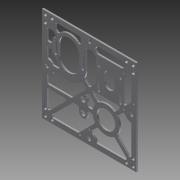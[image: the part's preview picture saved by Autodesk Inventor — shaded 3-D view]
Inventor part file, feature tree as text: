
AUTODESK INVENTOR PART (.ipt)
format: ipt  version: 2012 (Build 160160000, 160)  size: 569,856 bytes
history: native  units: in
note: dims shown in document units (in); Inventor stores cm internally (conversion verified against a paired STEP export)
features: fillet x6, hole x5, extrude x4, sketch x1, chamfer x1
ambient origin geometry x8: Origin, YZ Plane, XZ Plane, XY Plane, X Axis, Y Axis, Z Axis, Center Point
feature tree (17):
  sketch  "Sketch1"  dims[d0=4.5in d1=7.0in d2=7.0in d3=4.5in d4=1.375in d5=2.25in d6=2.25in d10=0.125in d12=0.125in d15=0.25in d16=0.75in d19=0.25in d20=0.75in d23=0.125in d24=0.25in d25=0.75in d26=0.125in d27=0.25in d28=0.25in d29=0.25in d30=0.75in d34=0.125in d35=0.25in d36=0.25in d37=0.25in d38=0.75in d39=0.125in d40=0.125in d47=0.125in d48=0.25in d49=0.25in d50=0.125in d51=0.75in d52=0.25in d87=1.5in d88=1.625in d89=1.5in d91=2.0in d95=0.75in d98=1.0in d99=1.0in d140=1.0in d141=1.0in d142=1.0in d143=1.0in d167=0.375in d168=0.375in d169=1.25in d171=6.25in d172=6.25in d173=0.375in d174=0.375in d177=3.625in d180=45.0deg d182=0.25in d183=0.25in d186=0.25in d188=0.25in d190=0.125in d195=0.125in d197=0.125in d198=0.25in d204=0.125in d205=0.125in d206=0.25in d207=0.125in d217=0.125in d218=3.5in d220=0.5in d221=1.375in d222=0.5in d223=1.375in d224=0.125in d225=0.0in d226=0.125in d227=0.2in d228=0.75in d229=0.375in d230=0.25in d231=0.5635in d232=1.0in d233=0.8108in d234=1.75in d235=1.0in d236=0.125in d237=0.75in d238=0.375in d239=0.25in d240=0.5635in d241=1.0in d242=0.8108in d243=1.875in d244=1.0in d245=0.125in d246=0.75in d247=0.375in d248=0.25in d249=0.5635in d250=1.0in d251=0.8108in d252=0.0625in d253=0.125in d254=45.0deg d255=0.5in d257=3.5in d258=0.5in d259=3.5in d260=0.5in d261=3.25in d262=3.5in d263=0.5in d264=0.25in d265=0.75in d266=0.375in d267=0.25in d268=0.5635in d269=1.0in d270=0.8108in d271=0.125in d273=0.125in d274=0.1in d275=0.375in d276=0.2in d277=0.75in d278=0.7874in d280=2.0in d281=0.3937in d283=1.0in d285=1.0in d286=0.0in d287=1.75in d288=1.75in d289=0.875in d290=0.0995in d291=0.199in d292=0.3125in d293=0.3125in d294=0.125in d295=0.366in d296=0.75in d297=0.375in d298=0.25in d299=0.5635in d300=1.0in d301=0.8108in d302=0.375in d303=0.375in d304=45.0deg d306=0.7874in d308=0.7874in d309=0.75in d310=0.75in d311=0.5in d312=0.8in d313=0.5in d314=1.05in d315=0.164in d316=1.6in d317=1.6in d318=2.0in d320=0.625in d322=0.5in d323=2.125in d324=2.5in d325=2.0in d326=0.125in d327=0.125in d328=0.125in d329=1.0in d330=0.0in d331=1.0in d332=0.375in d333=0.5in d334=0.375in d335=0.25in d336=1.0in d337=0.125in d338=0.375in d339=1.0in d340=1.0in d341=0.25in d342=0.375in d343=0.125in d344=1.0in d345=1.0in d346=0.375in d347=0.375in d348=1.0in d349=0.0in d350=0.125in d351=0.375in]
  extrude  "Extrusion8"  Depth=7.0in
  fillet  "Fillet3"  Radius=7.0in
  hole  "Hole5"  [1 undecoded]
  hole  "Hole6"  [1 undecoded]
  hole  "Hole7"  [1 undecoded]
  chamfer  "Chamfer1"  Distance=2.25in
  hole  "Hole8"  [1 undecoded]
  fillet  "Fillet4"  Radius=0.125in
  fillet  "Fillet5"  Radius=0.25in
  extrude  "Extrusion9"  Depth=0.75in
  fillet  "Fillet6"  Radius=0.25in
  hole  "Hole9"  [1 undecoded]
  fillet  "Fillet7"  Radius=0.125in
  extrude  "Extrusion10"  Depth=0.25in
  extrude  "Extrusion11"  Depth=0.75in
  fillet  "Fillet8"  Radius=0.125in
note: 5 required parameter values undecoded (feature->parameter linkage not recoverable at this tier; creation-order binding heuristic only, values carry confidence <= 0.55)
